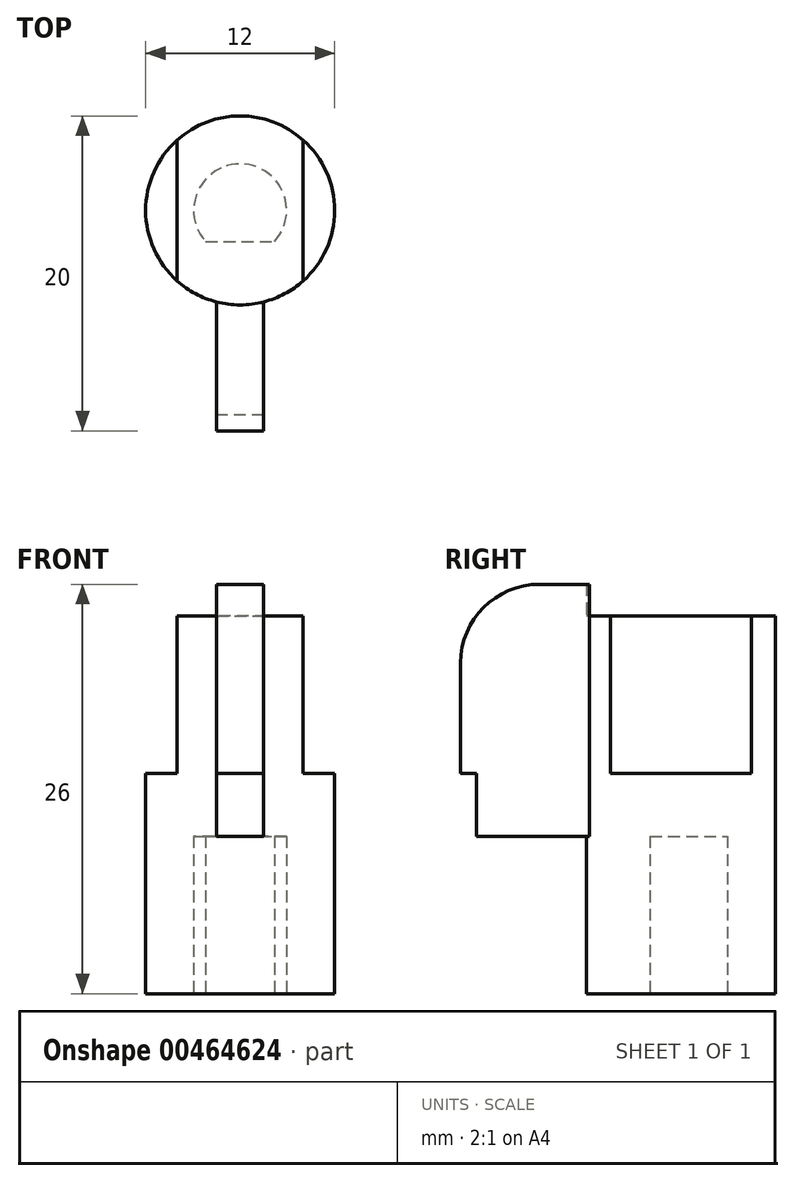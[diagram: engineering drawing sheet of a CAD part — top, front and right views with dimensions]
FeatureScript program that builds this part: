
annotation { "Feature Type Name" : "Feature", "Feature Type Description" : "" }
export const myFeature = defineFeature(function(context is Context, id is Id, definition is map)
    precondition{}
    {
        {
            var Q0;
            Q0=qCreatedBy(makeId("Top.planeOp"),FACE);
            var sketch = newSketch(context, id + "F0", { "sketchPlane" : qUnion([Q0])});
            skCircle(sketch, "E0", {"center": v(0, 0) * mm, "radius": 6 * mm});
            skArc(sketch, "E1", {"start": v(2.2, -1.97) * mm, "mid": v(0, 2.95) * mm, "end": v(-2.2, -1.97) * mm});
            skLineSegment(sketch, "E2", {"start": v(-2.2, -1.97) * mm, "end": v(2.2, -1.97) * mm});
            skPoint(sketch, "E3.orphan", {"position": v(0, 2.95) * mm});
            skPoint(sketch, "E4.start.orphan", {"position": v(0, 7.15) * mm});
            skSolve(sketch);
        }
        {
            var Q0;
            Q0=makeQuery(id+"F0.imprint","IMPRINT",FACE,{"disambiguationData":[TD([[makeQuery(id+"F0.imprint","IMPRINT",EDGE,{"derivedFrom":sQuery(id+"F0.wireOp",EDGE,"E0")}),1.0]])]});
            extrude(context, id + "F1", {"entities" : qUnion([Q0]), "depth" : 10 * mm});
        }
        {
            var Q0;
            Q0=makeQuery(id+"F1.opExtrude","CAP_FACE",FACE,{"disambiguationData":[OSD([sQuery(id+"F0.wireOp",EDGE,"E0"),sQuery(id+"F0.wireOp",EDGE,"E1"),sQuery(id+"F0.wireOp",EDGE,"E2")])],"isStart":false});
            var sketch = newSketch(context, id + "F2", { "sketchPlane" : qUnion([Q0])});
            skCircle(sketch, "E5", {"center": v(0, 0) * mm, "radius": 6 * mm});
            skSolve(sketch);
        }
        {
            var Q0;
            Q0 = qSketchRegion(id + "F2", true);
            extrude(context, id + "F3", {"entities" : qUnion([Q0]), "operationType" : NewBodyOperationType.ADD, "depth" : 6 * mm});
        }
        {
            var Q0;
            Q0=makeQuery(id+"F2.imprint","IMPRINT",FACE,{"disambiguationData":[TD([[makeQuery(id+"F2.imprint","IMPRINT",EDGE,{"derivedFrom":sQuery(id+"F2.wireOp",EDGE,"E5")}),1.0]])]});
            var sketch = newSketch(context, id + "F4", { "sketchPlane" : qUnion([Q0])});
            skLineSegment(sketch, "E6", {"start": v(0, 6.59) * mm, "end": v(0, -11.65) * mm, "construction": true});
            skCircle(sketch, "E7", {"center": v(0, 0) * mm, "radius": 6 * mm});
            skLineSegment(sketch, "E8", {"start": v(-1.5, -14) * mm, "end": v(1.5, -14) * mm});
            skLineSegment(sketch, "E9", {"start": v(1.5, -14) * mm, "end": v(1.5, -5.8) * mm});
            skLineSegment(sketch, "E10", {"start": v(-1.5, -14) * mm, "end": v(-1.5, -5.8) * mm});
            skSolve(sketch);
        }
        {
            var Q0;
            Q0=makeQuery(id+"F4.imprint","IMPRINT",FACE,{"disambiguationData":[TD([[makeQuery(id+"F4.imprint","IMPRINT",EDGE,{"derivedFrom":sQuery(id+"F4.wireOp",EDGE,"E8")}),1.0]])]});
            extrude(context, id + "F5", {"entities" : qUnion([Q0]), "depth" : 16 * mm, "offsetDistance" : 25 * mm});
        }
        {
            var Q0;
            Q0=makeQuery(id+"F3.opExtrude","CAP_FACE",FACE,{"disambiguationData":[OSD([sQuery(id+"F2.wireOp",EDGE,"E5")])],"isStart":false});
            var sketch = newSketch(context, id + "F6", { "sketchPlane" : qUnion([Q0])});
            skLineSegment(sketch, "E11", {"start": v(0, -15.72) * mm, "end": v(0, 10.66) * mm, "construction": true});
            skLineSegment(sketch, "E12", {"start": v(-4, -4.47) * mm, "end": v(-4, 4.47) * mm});
            skLineSegment(sketch, "E13", {"start": v(4, -4.47) * mm, "end": v(4, 4.47) * mm});
            skSolve(sketch);
        }
        {
            var Q0;
            {var subQ0=sQuery(id+"F6.wireOp",EDGE,"E12");Q0=makeQuery(id+"F6.imprint","IMPRINT",FACE,{"disambiguationData":[TD([[makeQuery(id+"F6.imprint","IMPRINT",EDGE,{"derivedFrom":subQ0}),-1.0]])]});}
            extrude(context, id + "F7", {"entities" : qUnion([Q0]), "operationType" : NewBodyOperationType.ADD, "depth" : 8 * mm});
        }
        {
            var Q0;
            Q0=makeQuery(id+"F5.opExtrude","SWEPT_FACE",FACE,{"disambiguationData":[OSD([sQuery(id+"F4.wireOp",EDGE,"E10")])]});
            var sketch = newSketch(context, id + "F8", { "sketchPlane" : qUnion([Q0])});
            skLineSegment(sketch, "E14.top", {"start": v(14, 10) * mm, "end": v(13, 10) * mm});
            skLineSegment(sketch, "E14.left", {"start": v(14, 14) * mm, "end": v(14, 10) * mm});
            skLineSegment(sketch, "E15", {"start": v(13, 14) * mm, "end": v(14, 14) * mm});
            skLineSegment(sketch, "E16", {"start": v(13, 10) * mm, "end": v(13, 14) * mm});
            skPoint(sketch, "E17.visualSharp", {"position": v(14, 26) * mm});
            skArc(sketch, "E17.filletArc", {"start": v(14, 21) * mm, "mid": v(12.54, 24.54) * mm, "end": v(9, 26) * mm});
            skPoint(sketch, "E18.visualSharp", {"position": v(5.8, 26) * mm});
            skLineSegment(sketch, "E19", {"start": v(14, 21) * mm, "end": v(14, 26) * mm});
            skLineSegment(sketch, "E20", {"start": v(9, 26) * mm, "end": v(14, 26) * mm});
            skSolve(sketch);
        }
        {
            var Q0;
            Q0=makeQuery(id+"F8.imprint","IMPRINT",FACE,{"disambiguationData":[TD([[makeQuery(id+"F8.imprint","IMPRINT",EDGE,{"derivedFrom":sQuery(id+"F8.wireOp",EDGE,"E17.filletArc")}),-1.0]])]});
            var Q1;
            Q1=makeQuery(id+"F8.imprint","IMPRINT",FACE,{"disambiguationData":[TD([[makeQuery(id+"F8.imprint","IMPRINT",EDGE,{"derivedFrom":sQuery(id+"F8.wireOp",EDGE,"E14.top")}),-1.0]])]});
            var Q2;
            Q2=makeQuery(id+"F8.imprint","IMPRINT",FACE,{"disambiguationData":[TD([[makeQuery(id+"F8.imprint","IMPRINT",EDGE,{"derivedFrom":sQuery(id+"F8.wireOp",EDGE,"E18.filletArc")}),-1.0]])]});
            extrude(context, id + "F9", {"entities" : qUnion([Q0, Q1, Q2]), "operationType" : NewBodyOperationType.REMOVE, "endBound" : BoundingType.THROUGH_ALL, "oppositeDirection" : true, "depth" : 25 * mm});
        }
        {
            var Q0;
            {var subQ0=sQuery(id+"F6.wireOp",EDGE,"E13");Q0=makeQuery(id+"F6.imprint","IMPRINT",FACE,{"disambiguationData":[TD([[makeQuery(id+"F6.imprint","IMPRINT",EDGE,{"derivedFrom":subQ0}),-1.0]])]});}
            var Q1;
            {var subQ0=sQuery(id+"F6.wireOp",EDGE,"E12");Q1=makeQuery(id+"F6.imprint","IMPRINT",FACE,{"disambiguationData":[TD([[makeQuery(id+"F6.imprint","IMPRINT",EDGE,{"derivedFrom":subQ0}),1.0]])]});}
            extrude(context, id + "F10", {"entities" : qUnion([Q0, Q1]), "operationType" : NewBodyOperationType.REMOVE, "oppositeDirection" : true, "depth" : 2 * mm, "offsetDistance" : 25 * mm});
        }
    });
